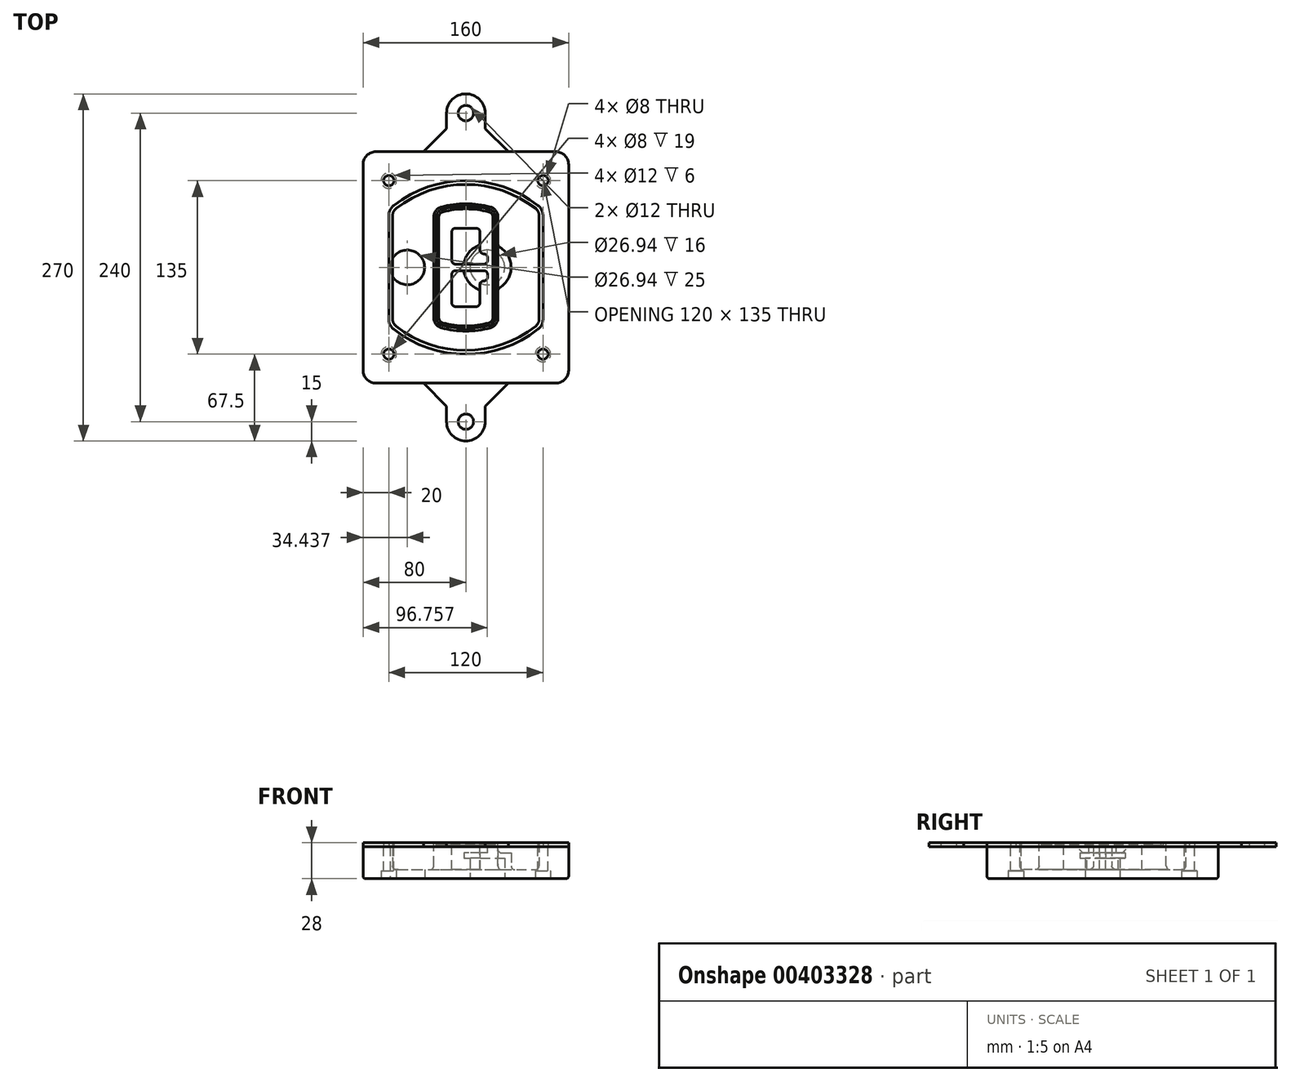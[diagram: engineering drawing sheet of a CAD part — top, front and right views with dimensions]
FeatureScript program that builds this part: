
annotation { "Feature Type Name" : "Feature", "Feature Type Description" : "" }
export const myFeature = defineFeature(function(context is Context, id is Id, definition is map)
    precondition{}
    {
        {
            var Q0;
            Q0=qCreatedBy(makeId("Top.planeOp"),FACE);
            var sketch = newSketch(context, id + "F0", { "sketchPlane" : qUnion([Q0])});
            skPoint(sketch, "E0.rect.middle", {"position": v(0, 0) * mm});
            skLineSegment(sketch, "E1.bottom", {"start": v(-70, -90) * mm, "end": v(70, -90) * mm});
            skLineSegment(sketch, "E1.top", {"start": v(-70, 90) * mm, "end": v(70, 90) * mm});
            skLineSegment(sketch, "E1.left", {"start": v(-80, -80) * mm, "end": v(-80, 80) * mm});
            skLineSegment(sketch, "E1.right", {"start": v(80, -80) * mm, "end": v(80, 80) * mm});
            skLineSegment(sketch, "E2", {"start": v(-80, 90) * mm, "end": v(80, -90) * mm, "construction": true});
            skLineSegment(sketch, "E3", {"start": v(80, 90) * mm, "end": v(-80, -90) * mm, "construction": true});
            skCircle(sketch, "E4", {"center": v(-60, 67.5) * mm, "radius": 4 * mm});
            skCircle(sketch, "E5", {"center": v(60, 67.5) * mm, "radius": 4 * mm});
            skCircle(sketch, "E6", {"center": v(60, -67.5) * mm, "radius": 4 * mm});
            skCircle(sketch, "E7", {"center": v(-60, -67.5) * mm, "radius": 4 * mm});
            skLineSegment(sketch, "E8", {"start": v(-60, 67.5) * mm, "end": v(60, 67.5) * mm, "construction": true});
            skLineSegment(sketch, "E9", {"start": v(60, 67.5) * mm, "end": v(60, -67.5) * mm, "construction": true});
            skLineSegment(sketch, "E10", {"start": v(60, -67.5) * mm, "end": v(-60, -67.5) * mm, "construction": true});
            skLineSegment(sketch, "E11", {"start": v(-60, -67.5) * mm, "end": v(-60, 67.5) * mm, "construction": true});
            skLineSegment(sketch, "E12", {"start": v(-60, 40.3) * mm, "end": v(-60, -40.3) * mm});
            skLineSegment(sketch, "E13", {"start": v(60, 40.3) * mm, "end": v(60, -40.3) * mm});
            skArc(sketch, "E14", {"start": v(56.15, 48.18) * mm, "mid": v(0, 67.5) * mm, "end": v(-56.15, 48.18) * mm});
            skArc(sketch, "E15", {"start": v(-56.15, -48.18) * mm, "mid": v(0, -67.5) * mm, "end": v(56.15, -48.18) * mm});
            skLineSegment(sketch, "E16", {"start": v(-60, 0) * mm, "end": v(60, 0) * mm, "construction": true});
            skPoint(sketch, "E17.visualSharp", {"position": v(-60, -45) * mm});
            skArc(sketch, "E17.filletArc", {"start": v(-60, -40.3) * mm, "mid": v(-58.99, -44.68) * mm, "end": v(-56.15, -48.18) * mm});
            skPoint(sketch, "E18.visualSharp", {"position": v(-60, 45) * mm});
            skArc(sketch, "E18.filletArc", {"start": v(-56.15, 48.18) * mm, "mid": v(-58.99, 44.68) * mm, "end": v(-60, 40.3) * mm});
            skPoint(sketch, "E19.visualSharp", {"position": v(60, 45) * mm});
            skArc(sketch, "E19.filletArc", {"start": v(60, 40.3) * mm, "mid": v(58.99, 44.68) * mm, "end": v(56.15, 48.18) * mm});
            skPoint(sketch, "E20.visualSharp", {"position": v(60, -45) * mm});
            skArc(sketch, "E20.filletArc", {"start": v(56.15, -48.18) * mm, "mid": v(58.99, -44.68) * mm, "end": v(60, -40.3) * mm});
            skPoint(sketch, "E21.visualSharp", {"position": v(-80, 90) * mm});
            skArc(sketch, "E21.filletArc", {"start": v(-70, 90) * mm, "mid": v(-77.07, 87.07) * mm, "end": v(-80, 80) * mm});
            skPoint(sketch, "E22.visualSharp", {"position": v(80, 90) * mm});
            skArc(sketch, "E22.filletArc", {"start": v(80, 80) * mm, "mid": v(77.07, 87.07) * mm, "end": v(70, 90) * mm});
            skPoint(sketch, "E23.visualSharp", {"position": v(80, -90) * mm});
            skArc(sketch, "E23.filletArc", {"start": v(70, -90) * mm, "mid": v(77.07, -87.07) * mm, "end": v(80, -80) * mm});
            skPoint(sketch, "E24.visualSharp", {"position": v(-80, -90) * mm});
            skArc(sketch, "E24.filletArc", {"start": v(-80, -80) * mm, "mid": v(-77.07, -87.07) * mm, "end": v(-70, -90) * mm});
            skArc(sketch, "E25.0", {"start": v(57, 40.3) * mm, "mid": v(56.3, 43.36) * mm, "end": v(54.3, 45.81) * mm});
            skLineSegment(sketch, "E25.1", {"start": v(57, 40.3) * mm, "end": v(57, -40.3) * mm});
            skArc(sketch, "E25.2", {"start": v(54.3, -45.81) * mm, "mid": v(56.3, -43.36) * mm, "end": v(57, -40.3) * mm});
            skArc(sketch, "E25.3", {"start": v(-54.3, -45.81) * mm, "mid": v(0, -64.5) * mm, "end": v(54.3, -45.81) * mm});
            skArc(sketch, "E25.4", {"start": v(-57, -40.3) * mm, "mid": v(-56.3, -43.36) * mm, "end": v(-54.3, -45.81) * mm});
            skArc(sketch, "E25.5", {"start": v(54.3, 45.81) * mm, "mid": v(0, 64.5) * mm, "end": v(-54.3, 45.81) * mm});
            skLineSegment(sketch, "E25.6", {"start": v(-57, 40.3) * mm, "end": v(-57, -40.3) * mm});
            skArc(sketch, "E25.7", {"start": v(-54.3, 45.81) * mm, "mid": v(-56.3, 43.36) * mm, "end": v(-57, 40.3) * mm});
            skArc(sketch, "E26.0", {"start": v(-58.62, 51.33) * mm, "mid": v(-62.58, 46.43) * mm, "end": v(-64, 40.3) * mm});
            skArc(sketch, "E26.1", {"start": v(58.62, 51.33) * mm, "mid": v(0, 71.5) * mm, "end": v(-58.62, 51.33) * mm});
            skArc(sketch, "E26.2", {"start": v(64, 40.3) * mm, "mid": v(62.58, 46.43) * mm, "end": v(58.62, 51.33) * mm});
            skLineSegment(sketch, "E26.3", {"start": v(64, 40.3) * mm, "end": v(64, -40.3) * mm});
            skArc(sketch, "E26.4", {"start": v(58.62, -51.33) * mm, "mid": v(62.58, -46.43) * mm, "end": v(64, -40.3) * mm});
            skLineSegment(sketch, "E26.5", {"start": v(-64, 40.3) * mm, "end": v(-64, -40.3) * mm});
            skArc(sketch, "E26.6", {"start": v(-58.62, -51.33) * mm, "mid": v(0, -71.5) * mm, "end": v(58.62, -51.33) * mm});
            skArc(sketch, "E26.7", {"start": v(-64, -40.3) * mm, "mid": v(-62.58, -46.43) * mm, "end": v(-58.62, -51.33) * mm});
            skSolve(sketch);
        }
        {
            var Q0;
            Q0=makeQuery(id+"F0.imprint","IMPRINT",FACE,{"disambiguationData":[TD([[makeQuery(id+"F0.imprint","IMPRINT",EDGE,{"derivedFrom":sQuery(id+"F0.wireOp",EDGE,"E1.bottom")}),1.0]])]});
            var Q1;
            Q1=makeQuery(id+"F0.imprint","IMPRINT",FACE,{"disambiguationData":[TD([[makeQuery(id+"F0.imprint","IMPRINT",EDGE,{"derivedFrom":sQuery(id+"F0.wireOp",EDGE,"E12")}),1.0]])]});
            var Q2;
            Q2=makeQuery(id+"F0.imprint","IMPRINT",FACE,{"disambiguationData":[TD([[makeQuery(id+"F0.imprint","IMPRINT",EDGE,{"derivedFrom":sQuery(id+"F0.wireOp",EDGE,"E25.0")}),1.0]])]});
            var Q3;
            Q3=makeQuery(id+"F0.imprint","IMPRINT",FACE,{"disambiguationData":[TD([[makeQuery(id+"F0.imprint","IMPRINT",EDGE,{"derivedFrom":sQuery(id+"F0.wireOp",EDGE,"E12")}),-1.0]])]});
            extrude(context, id + "F1", {"entities" : qUnion([Q0, Q1, Q2, Q3]), "oppositeDirection" : true, "depth" : 25 * mm});
        }
        {
            var Q0;
            Q0=makeQuery(id+"F0.imprint","IMPRINT",FACE,{"disambiguationData":[TD([[makeQuery(id+"F0.imprint","IMPRINT",EDGE,{"derivedFrom":sQuery(id+"F0.wireOp",EDGE,"E12")}),1.0]])]});
            extrude(context, id + "F2", {"entities" : qUnion([Q0]), "operationType" : NewBodyOperationType.ADD, "depth" : 3 * mm});
        }
        {
            var Q0;
            Q0=makeQuery(id+"F0.imprint","IMPRINT",FACE,{"disambiguationData":[TD([[makeQuery(id+"F0.imprint","IMPRINT",EDGE,{"derivedFrom":sQuery(id+"F0.wireOp",EDGE,"E25.0")}),1.0]])]});
            extrude(context, id + "F3", {"entities" : qUnion([Q0]), "operationType" : NewBodyOperationType.REMOVE, "oppositeDirection" : true, "depth" : 18 * mm});
        }
        {
            var Q0;
            Q0=makeQuery(id+"F2.opExtrude","CAP_FACE",FACE,{"disambiguationData":[OSD([sQuery(id+"F0.wireOp",EDGE,"E12"),sQuery(id+"F0.wireOp",EDGE,"E13"),sQuery(id+"F0.wireOp",EDGE,"E14"),sQuery(id+"F0.wireOp",EDGE,"E15"),sQuery(id+"F0.wireOp",EDGE,"E17.filletArc"),sQuery(id+"F0.wireOp",EDGE,"E18.filletArc"),sQuery(id+"F0.wireOp",EDGE,"E19.filletArc"),sQuery(id+"F0.wireOp",EDGE,"E20.filletArc"),sQuery(id+"F0.wireOp",EDGE,"E25.0"),sQuery(id+"F0.wireOp",EDGE,"E25.1"),sQuery(id+"F0.wireOp",EDGE,"E25.2"),sQuery(id+"F0.wireOp",EDGE,"E25.3"),sQuery(id+"F0.wireOp",EDGE,"E25.4"),sQuery(id+"F0.wireOp",EDGE,"E25.5"),sQuery(id+"F0.wireOp",EDGE,"E25.6"),sQuery(id+"F0.wireOp",EDGE,"E25.7")])],"isStart":false});
            var sketch = newSketch(context, id + "F4", { "sketchPlane" : qUnion([Q0])});
            skArc(sketch, "E27.0", {"start": v(-19.08, -46.97) * mm, "mid": v(0, -49.5) * mm, "end": v(19.08, -46.97) * mm});
            skArc(sketch, "E28.0", {"start": v(19.08, 46.97) * mm, "mid": v(0, 49.5) * mm, "end": v(-19.08, 46.97) * mm});
            skLineSegment(sketch, "E29", {"start": v(-25, 39.25) * mm, "end": v(-25, -39.25) * mm});
            skLineSegment(sketch, "E30", {"start": v(25, 39.25) * mm, "end": v(25, -39.25) * mm});
            skLineSegment(sketch, "E31", {"start": v(-25, 45.1) * mm, "end": v(25, 45.1) * mm, "construction": true});
            skLineSegment(sketch, "E32", {"start": v(-25, -45.1) * mm, "end": v(25, -45.1) * mm, "construction": true});
            skPoint(sketch, "E33.visualSharp", {"position": v(-25, 45.1) * mm});
            skArc(sketch, "E33.filletArc", {"start": v(-19.08, 46.97) * mm, "mid": v(-23.35, 44.11) * mm, "end": v(-25, 39.25) * mm});
            skPoint(sketch, "E34.visualSharp", {"position": v(25, 45.1) * mm});
            skArc(sketch, "E34.filletArc", {"start": v(25, 39.25) * mm, "mid": v(23.35, 44.11) * mm, "end": v(19.08, 46.97) * mm});
            skPoint(sketch, "E35.visualSharp", {"position": v(25, -45.1) * mm});
            skArc(sketch, "E35.filletArc", {"start": v(19.08, -46.97) * mm, "mid": v(23.35, -44.11) * mm, "end": v(25, -39.25) * mm});
            skPoint(sketch, "E36.visualSharp", {"position": v(-25, -45.1) * mm});
            skArc(sketch, "E36.filletArc", {"start": v(-25, -39.25) * mm, "mid": v(-23.35, -44.11) * mm, "end": v(-19.08, -46.97) * mm});
            skArc(sketch, "E37.0", {"start": v(54.3, 45.81) * mm, "mid": v(0, 64.5) * mm, "end": v(-54.3, 45.81) * mm});
            skArc(sketch, "E37.1", {"start": v(-54.3, 45.81) * mm, "mid": v(-56.3, 43.36) * mm, "end": v(-57, 40.3) * mm});
            skLineSegment(sketch, "E37.2", {"start": v(-57, 40.3) * mm, "end": v(-57, -40.3) * mm});
            skArc(sketch, "E37.3", {"start": v(-57, -40.3) * mm, "mid": v(-56.3, -43.36) * mm, "end": v(-54.3, -45.81) * mm});
            skArc(sketch, "E37.4", {"start": v(-54.3, -45.81) * mm, "mid": v(0, -64.5) * mm, "end": v(54.3, -45.81) * mm});
            skArc(sketch, "E37.5", {"start": v(54.3, -45.81) * mm, "mid": v(56.3, -43.36) * mm, "end": v(57, -40.3) * mm});
            skLineSegment(sketch, "E37.6", {"start": v(57, 40.3) * mm, "end": v(57, -40.3) * mm});
            skArc(sketch, "E37.7", {"start": v(57, 40.3) * mm, "mid": v(56.3, 43.36) * mm, "end": v(54.3, 45.81) * mm});
            skLineSegment(sketch, "E38.0", {"start": v(23, 39.25) * mm, "end": v(23, -39.25) * mm});
            skArc(sketch, "E38.1", {"start": v(18.56, -45.04) * mm, "mid": v(21.76, -42.9) * mm, "end": v(23, -39.25) * mm});
            skArc(sketch, "E38.2", {"start": v(-18.56, -45.04) * mm, "mid": v(0, -47.5) * mm, "end": v(18.56, -45.04) * mm});
            skArc(sketch, "E38.3", {"start": v(-23, -39.25) * mm, "mid": v(-21.76, -42.9) * mm, "end": v(-18.56, -45.04) * mm});
            skLineSegment(sketch, "E38.4", {"start": v(-23, 39.25) * mm, "end": v(-23, -39.25) * mm});
            skArc(sketch, "E38.5", {"start": v(23, 39.25) * mm, "mid": v(21.76, 42.9) * mm, "end": v(18.56, 45.04) * mm});
            skArc(sketch, "E38.6", {"start": v(-18.56, 45.04) * mm, "mid": v(-21.76, 42.9) * mm, "end": v(-23, 39.25) * mm});
            skArc(sketch, "E38.7", {"start": v(18.56, 45.04) * mm, "mid": v(0, 47.5) * mm, "end": v(-18.56, 45.04) * mm});
            skArc(sketch, "E39.0", {"start": v(21, 39.25) * mm, "mid": v(20.18, 41.68) * mm, "end": v(18.04, 43.1) * mm});
            skLineSegment(sketch, "E39.1", {"start": v(21, 39.25) * mm, "end": v(21, -39.25) * mm});
            skArc(sketch, "E39.2", {"start": v(18.04, -43.1) * mm, "mid": v(20.18, -41.68) * mm, "end": v(21, -39.25) * mm});
            skArc(sketch, "E39.3", {"start": v(-18.04, -43.1) * mm, "mid": v(0, -45.5) * mm, "end": v(18.04, -43.1) * mm});
            skArc(sketch, "E39.4", {"start": v(-21, -39.25) * mm, "mid": v(-20.18, -41.68) * mm, "end": v(-18.04, -43.1) * mm});
            skArc(sketch, "E39.5", {"start": v(18.04, 43.1) * mm, "mid": v(0, 45.5) * mm, "end": v(-18.04, 43.1) * mm});
            skLineSegment(sketch, "E39.6", {"start": v(-21, 39.25) * mm, "end": v(-21, -39.25) * mm});
            skArc(sketch, "E39.7", {"start": v(-18.04, 43.1) * mm, "mid": v(-20.18, 41.68) * mm, "end": v(-21, 39.25) * mm});
            skLineSegment(sketch, "E40", {"start": v(-25, 0) * mm, "end": v(25, 0) * mm, "construction": true});
            skLineSegment(sketch, "E41", {"start": v(-11, 5.5) * mm, "end": v(-11, 27.5) * mm});
            skLineSegment(sketch, "E42", {"start": v(-8, 30.5) * mm, "end": v(8, 30.5) * mm});
            skLineSegment(sketch, "E43", {"start": v(11, 27.5) * mm, "end": v(11, 13.5) * mm});
            skLineSegment(sketch, "E44", {"start": v(14, 10.5) * mm, "end": v(14, 10.5) * mm});
            skLineSegment(sketch, "E45", {"start": v(17, 7.5) * mm, "end": v(17, 5.5) * mm});
            skLineSegment(sketch, "E46", {"start": v(14, 2.5) * mm, "end": v(-8, 2.5) * mm});
            skPoint(sketch, "E47.visualSharp", {"position": v(-11, 30.5) * mm});
            skArc(sketch, "E47.filletArc", {"start": v(-8, 30.5) * mm, "mid": v(-10.12, 29.62) * mm, "end": v(-11, 27.5) * mm});
            skPoint(sketch, "E48.visualSharp", {"position": v(11, 30.5) * mm});
            skArc(sketch, "E48.filletArc", {"start": v(11, 27.5) * mm, "mid": v(10.12, 29.62) * mm, "end": v(8, 30.5) * mm});
            skPoint(sketch, "E49.visualSharp", {"position": v(11, 10.5) * mm});
            skArc(sketch, "E49.filletArc", {"start": v(11, 13.5) * mm, "mid": v(11.88, 11.38) * mm, "end": v(14, 10.5) * mm});
            skPoint(sketch, "E50.visualSharp", {"position": v(17, 10.5) * mm});
            skArc(sketch, "E50.filletArc", {"start": v(17, 7.5) * mm, "mid": v(16.12, 9.62) * mm, "end": v(14, 10.5) * mm});
            skPoint(sketch, "E51.visualSharp", {"position": v(17, 2.5) * mm});
            skArc(sketch, "E51.filletArc", {"start": v(14, 2.5) * mm, "mid": v(16.12, 3.38) * mm, "end": v(17, 5.5) * mm});
            skPoint(sketch, "E52.visualSharp", {"position": v(-11, 2.5) * mm});
            skArc(sketch, "E52.filletArc", {"start": v(-11, 5.5) * mm, "mid": v(-10.12, 3.38) * mm, "end": v(-8, 2.5) * mm});
            skLineSegment(sketch, "E53.0.MirrorCS", {"start": v(14, -2.5) * mm, "end": v(-8, -2.5) * mm});
            skArc(sketch, "E54.0.MirrorCS", {"start": v(-11, -5.5) * mm, "mid": v(-10.12, -3.38) * mm, "end": v(-8, -2.5) * mm});
            skLineSegment(sketch, "E55.0.MirrorCS", {"start": v(-11, -5.5) * mm, "end": v(-11, -27.5) * mm});
            skArc(sketch, "E56.0.MirrorCS", {"start": v(-8, -30.5) * mm, "mid": v(-10.12, -29.62) * mm, "end": v(-11, -27.5) * mm});
            skLineSegment(sketch, "E57.0.MirrorCS", {"start": v(-8, -30.5) * mm, "end": v(8, -30.5) * mm});
            skArc(sketch, "E58.0.MirrorCS", {"start": v(11, -27.5) * mm, "mid": v(10.12, -29.62) * mm, "end": v(8, -30.5) * mm});
            skLineSegment(sketch, "E59.0.MirrorCS", {"start": v(11, -27.5) * mm, "end": v(11, -13.5) * mm});
            skArc(sketch, "E60.0.MirrorCS", {"start": v(11, -13.5) * mm, "mid": v(11.88, -11.38) * mm, "end": v(14, -10.5) * mm});
            skArc(sketch, "E61.0.MirrorCS", {"start": v(17, -7.5) * mm, "mid": v(16.12, -9.62) * mm, "end": v(14, -10.5) * mm});
            skLineSegment(sketch, "E62.0.MirrorCS", {"start": v(17, -7.5) * mm, "end": v(17, -5.5) * mm});
            skArc(sketch, "E63.0.MirrorCS", {"start": v(14, -2.5) * mm, "mid": v(16.12, -3.38) * mm, "end": v(17, -5.5) * mm});
            skSolve(sketch);
        }
        {
            var Q0;
            Q0=makeQuery(id+"F4.imprint","IMPRINT",FACE,{"disambiguationData":[TD([[makeQuery(id+"F4.imprint","IMPRINT",EDGE,{"derivedFrom":sQuery(id+"F4.wireOp",EDGE,"E27.0")}),1.0]])]});
            var Q1;
            Q1=makeQuery(id+"F4.imprint","IMPRINT",FACE,{"disambiguationData":[TD([[makeQuery(id+"F4.imprint","IMPRINT",EDGE,{"derivedFrom":sQuery(id+"F4.wireOp",EDGE,"E38.0")}),-1.0]])]});
            var Q2;
            Q2=makeQuery(id+"F4.imprint","IMPRINT",FACE,{"disambiguationData":[TD([[makeQuery(id+"F4.imprint","IMPRINT",EDGE,{"derivedFrom":sQuery(id+"F4.wireOp",EDGE,"E39.0")}),1.0]])]});
            extrude(context, id + "F5", {"entities" : qUnion([Q0, Q1, Q2]), "operationType" : NewBodyOperationType.ADD, "endBound" : BoundingType.UP_TO_NEXT, "oppositeDirection" : true, "depth" : 25 * mm});
        }
        {
            var Q0;
            Q0=makeQuery(id+"F4.imprint","IMPRINT",FACE,{"disambiguationData":[TD([[makeQuery(id+"F4.imprint","IMPRINT",EDGE,{"derivedFrom":sQuery(id+"F4.wireOp",EDGE,"E38.0")}),-1.0]])]});
            extrude(context, id + "F6", {"entities" : qUnion([Q0]), "operationType" : NewBodyOperationType.REMOVE, "oppositeDirection" : true, "depth" : 2 * mm});
        }
        {
            var Q0;
            Q0=makeQuery(id+"F1.opExtrude","CAP_FACE",FACE,{"disambiguationData":[OSD([sQuery(id+"F0.wireOp",EDGE,"E1.bottom"),sQuery(id+"F0.wireOp",EDGE,"E1.top"),sQuery(id+"F0.wireOp",EDGE,"E1.left"),sQuery(id+"F0.wireOp",EDGE,"E1.right"),sQuery(id+"F0.wireOp",EDGE,"E4"),sQuery(id+"F0.wireOp",EDGE,"E5"),sQuery(id+"F0.wireOp",EDGE,"E6"),sQuery(id+"F0.wireOp",EDGE,"E7"),sQuery(id+"F0.wireOp",EDGE,"E21.filletArc"),sQuery(id+"F0.wireOp",EDGE,"E22.filletArc"),sQuery(id+"F0.wireOp",EDGE,"E23.filletArc"),sQuery(id+"F0.wireOp",EDGE,"E24.filletArc")])],"isStart":false});
            var sketch = newSketch(context, id + "F7", { "sketchPlane" : qUnion([Q0])});
            skCircle(sketch, "E64", {"center": v(16.76, 0) * mm, "radius": 13.47 * mm});
            skCircle(sketch, "E65", {"center": v(-45.56, 0) * mm, "radius": 13.47 * mm});
            skLineSegment(sketch, "E66", {"start": v(80, 0) * mm, "end": v(-80, 0) * mm});
            skCircle(sketch, "E67", {"center": v(16.76, 0) * mm, "radius": 18.47 * mm});
            skCircle(sketch, "E68", {"center": v(60, -67.5) * mm, "radius": 6 * mm});
            skCircle(sketch, "E69", {"center": v(-60, -67.5) * mm, "radius": 6 * mm});
            skCircle(sketch, "E70", {"center": v(-60, 67.5) * mm, "radius": 6 * mm});
            skCircle(sketch, "E71", {"center": v(60, 67.5) * mm, "radius": 6 * mm});
            skSolve(sketch);
        }
        {
            var Q0;
            {var subQ1=sQuery(id+"F7.wireOp",EDGE,"E66");var subQ4=sQuery(id+"F7.wireOp",EDGE,"E64");var subQ6=makeQuery(id+"F7.imprint","INTERSECT",VERTEX,{"disambiguationData":[OD(0.0)],"derivedFrom":[subQ4,subQ1]});Q0=makeQuery(id+"F7.imprint","IMPRINT",FACE,{"disambiguationData":[TD([[makeQuery(id+"F7.imprint","IMPRINT",EDGE,{"disambiguationData":[TD([[subQ6,-1.0]])],"derivedFrom":subQ4}),-1.0]])]});}
            var Q1;
            {var subQ0=sQuery(id+"F7.wireOp",EDGE,"E66");var subQ1=sQuery(id+"F7.wireOp",EDGE,"E64");var subQ3=makeQuery(id+"F7.imprint","INTERSECT",VERTEX,{"disambiguationData":[OD(0.0)],"derivedFrom":[subQ1,subQ0]});Q1=makeQuery(id+"F7.imprint","IMPRINT",FACE,{"disambiguationData":[TD([[makeQuery(id+"F7.imprint","IMPRINT",EDGE,{"disambiguationData":[TD([[subQ3,-1.0]])],"derivedFrom":subQ1}),1.0]])]});}
            var Q2;
            {var subQ0=sQuery(id+"F7.wireOp",EDGE,"E66");var subQ1=sQuery(id+"F7.wireOp",EDGE,"E64");var subQ3=makeQuery(id+"F7.imprint","INTERSECT",VERTEX,{"disambiguationData":[OD(0.0)],"derivedFrom":[subQ1,subQ0]});Q2=makeQuery(id+"F7.imprint","IMPRINT",FACE,{"disambiguationData":[TD([[makeQuery(id+"F7.imprint","IMPRINT",EDGE,{"disambiguationData":[TD([[subQ3,1.0]])],"derivedFrom":subQ1}),1.0]])]});}
            var Q3;
            {var subQ1=sQuery(id+"F7.wireOp",EDGE,"E66");var subQ4=sQuery(id+"F7.wireOp",EDGE,"E64");var subQ6=makeQuery(id+"F7.imprint","INTERSECT",VERTEX,{"disambiguationData":[OD(0.0)],"derivedFrom":[subQ4,subQ1]});Q3=makeQuery(id+"F7.imprint","IMPRINT",FACE,{"disambiguationData":[TD([[makeQuery(id+"F7.imprint","IMPRINT",EDGE,{"disambiguationData":[TD([[subQ6,1.0]])],"derivedFrom":subQ4}),-1.0]])]});}
            extrude(context, id + "F8", {"entities" : qUnion([Q0, Q1, Q2, Q3]), "operationType" : NewBodyOperationType.ADD, "oppositeDirection" : true, "depth" : 20 * mm});
        }
        {
            var Q0;
            {var subQ0=sQuery(id+"F7.wireOp",EDGE,"E66");var subQ1=sQuery(id+"F7.wireOp",EDGE,"E64");var subQ3=makeQuery(id+"F7.imprint","INTERSECT",VERTEX,{"disambiguationData":[OD(0.0)],"derivedFrom":[subQ1,subQ0]});Q0=makeQuery(id+"F7.imprint","IMPRINT",FACE,{"disambiguationData":[TD([[makeQuery(id+"F7.imprint","IMPRINT",EDGE,{"disambiguationData":[TD([[subQ3,-1.0]])],"derivedFrom":subQ1}),1.0]])]});}
            var Q1;
            {var subQ0=sQuery(id+"F7.wireOp",EDGE,"E66");var subQ1=sQuery(id+"F7.wireOp",EDGE,"E64");var subQ3=makeQuery(id+"F7.imprint","INTERSECT",VERTEX,{"disambiguationData":[OD(0.0)],"derivedFrom":[subQ1,subQ0]});Q1=makeQuery(id+"F7.imprint","IMPRINT",FACE,{"disambiguationData":[TD([[makeQuery(id+"F7.imprint","IMPRINT",EDGE,{"disambiguationData":[TD([[subQ3,1.0]])],"derivedFrom":subQ1}),1.0]])]});}
            extrude(context, id + "F9", {"entities" : qUnion([Q0, Q1]), "operationType" : NewBodyOperationType.REMOVE, "oppositeDirection" : true, "depth" : 16 * mm});
        }
        {
            var Q0;
            {var subQ0=sQuery(id+"F7.wireOp",EDGE,"E66");var subQ1=sQuery(id+"F7.wireOp",EDGE,"E65");var subQ3=makeQuery(id+"F7.imprint","INTERSECT",VERTEX,{"disambiguationData":[OD(0.0)],"derivedFrom":[subQ1,subQ0]});Q0=makeQuery(id+"F7.imprint","IMPRINT",FACE,{"disambiguationData":[TD([[makeQuery(id+"F7.imprint","IMPRINT",EDGE,{"disambiguationData":[TD([[subQ3,-1.0]])],"derivedFrom":subQ1}),1.0]])]});}
            var Q1;
            {var subQ0=sQuery(id+"F7.wireOp",EDGE,"E66");var subQ1=sQuery(id+"F7.wireOp",EDGE,"E65");var subQ3=makeQuery(id+"F7.imprint","INTERSECT",VERTEX,{"disambiguationData":[OD(0.0)],"derivedFrom":[subQ1,subQ0]});Q1=makeQuery(id+"F7.imprint","IMPRINT",FACE,{"disambiguationData":[TD([[makeQuery(id+"F7.imprint","IMPRINT",EDGE,{"disambiguationData":[TD([[subQ3,1.0]])],"derivedFrom":subQ1}),1.0]])]});}
            extrude(context, id + "F10", {"entities" : qUnion([Q0, Q1]), "operationType" : NewBodyOperationType.REMOVE, "oppositeDirection" : true, "depth" : 25 * mm});
        }
        {
            var Q0;
            Q0=makeQuery(id+"F7.imprint","IMPRINT",FACE,{"disambiguationData":[TD([[makeQuery(id+"F7.imprint","IMPRINT",EDGE,{"derivedFrom":sQuery(id+"F7.wireOp",EDGE,"E68")}),1.0]])]});
            var Q1;
            Q1=makeQuery(id+"F7.imprint","IMPRINT",FACE,{"disambiguationData":[TD([[makeQuery(id+"F7.imprint","IMPRINT",EDGE,{"derivedFrom":makeQuery(id+"F1.opExtrude","CAP_EDGE",EDGE,{"disambiguationData":[OSD([sQuery(id+"F0.wireOp",EDGE,"E5")])],"isStart":false})}),-1.0]])]});
            var Q2;
            Q2=makeQuery(id+"F7.imprint","IMPRINT",FACE,{"disambiguationData":[TD([[makeQuery(id+"F7.imprint","IMPRINT",EDGE,{"derivedFrom":sQuery(id+"F7.wireOp",EDGE,"E69")}),1.0]])]});
            var Q3;
            Q3=makeQuery(id+"F7.imprint","IMPRINT",FACE,{"disambiguationData":[TD([[makeQuery(id+"F7.imprint","IMPRINT",EDGE,{"derivedFrom":makeQuery(id+"F1.opExtrude","CAP_EDGE",EDGE,{"disambiguationData":[OSD([sQuery(id+"F0.wireOp",EDGE,"E4")])],"isStart":false})}),-1.0]])]});
            var Q4;
            Q4=makeQuery(id+"F7.imprint","IMPRINT",FACE,{"disambiguationData":[TD([[makeQuery(id+"F7.imprint","IMPRINT",EDGE,{"derivedFrom":sQuery(id+"F7.wireOp",EDGE,"E70")}),1.0]])]});
            var Q5;
            Q5=makeQuery(id+"F7.imprint","IMPRINT",FACE,{"disambiguationData":[TD([[makeQuery(id+"F7.imprint","IMPRINT",EDGE,{"derivedFrom":makeQuery(id+"F1.opExtrude","CAP_EDGE",EDGE,{"disambiguationData":[OSD([sQuery(id+"F0.wireOp",EDGE,"E7")])],"isStart":false})}),-1.0]])]});
            var Q6;
            Q6=makeQuery(id+"F7.imprint","IMPRINT",FACE,{"disambiguationData":[TD([[makeQuery(id+"F7.imprint","IMPRINT",EDGE,{"derivedFrom":sQuery(id+"F7.wireOp",EDGE,"E71")}),1.0]])]});
            var Q7;
            Q7=makeQuery(id+"F7.imprint","IMPRINT",FACE,{"disambiguationData":[TD([[makeQuery(id+"F7.imprint","IMPRINT",EDGE,{"derivedFrom":makeQuery(id+"F1.opExtrude","CAP_EDGE",EDGE,{"disambiguationData":[OSD([sQuery(id+"F0.wireOp",EDGE,"E6")])],"isStart":false})}),-1.0]])]});
            extrude(context, id + "F11", {"entities" : qUnion([Q0, Q1, Q2, Q3, Q4, Q5, Q6, Q7]), "operationType" : NewBodyOperationType.REMOVE, "oppositeDirection" : true, "depth" : 6 * mm});
        }
        {
            var Q0;
            Q0=makeQuery(id+"F9.boolean.opBoolean","COPY",FACE,{"derivedFrom":makeQuery(id+"F9.opExtrude","CAP_FACE",FACE,{"disambiguationData":[OSD([sQuery(id+"F7.wireOp",EDGE,"E64")])],"isStart":false})});
            var sketch = newSketch(context, id + "F12", { "sketchPlane" : qUnion([Q0])});
            skArc(sketch, "E72.0", {"start": v(11, 17.55) * mm, "mid": v(2.57, 11.82) * mm, "end": v(-1.54, 2.5) * mm});
            skArc(sketch, "E72.1", {"start": v(-1.54, -2.5) * mm, "mid": v(2.57, -11.82) * mm, "end": v(11, -17.55) * mm});
            skLineSegment(sketch, "E73", {"start": v(-1.54, -2.5) * mm, "end": v(14, -2.5) * mm});
            skLineSegment(sketch, "E74.0", {"start": v(14, 2.5) * mm, "end": v(-1.54, 2.5) * mm});
            skArc(sketch, "E74.1", {"start": v(14, 2.5) * mm, "mid": v(16.12, 3.38) * mm, "end": v(17, 5.5) * mm});
            skLineSegment(sketch, "E74.2", {"start": v(17, 7.5) * mm, "end": v(17, 5.5) * mm});
            skArc(sketch, "E74.3", {"start": v(17, 7.5) * mm, "mid": v(16.12, 9.62) * mm, "end": v(14, 10.5) * mm});
            skArc(sketch, "E74.4", {"start": v(11, 13.5) * mm, "mid": v(11.88, 11.38) * mm, "end": v(14, 10.5) * mm});
            skLineSegment(sketch, "E74.5", {"start": v(11, 17.55) * mm, "end": v(11, 13.5) * mm});
            skLineSegment(sketch, "E74.7", {"start": v(14, -2.5) * mm, "end": v(-1.54, -2.5) * mm});
            skArc(sketch, "E74.8", {"start": v(14, -2.5) * mm, "mid": v(16.12, -3.38) * mm, "end": v(17, -5.5) * mm});
            skLineSegment(sketch, "E74.9", {"start": v(17, -7.5) * mm, "end": v(17, -5.5) * mm});
            skArc(sketch, "E74.10", {"start": v(17, -7.5) * mm, "mid": v(16.12, -9.62) * mm, "end": v(14, -10.5) * mm});
            skArc(sketch, "E74.11", {"start": v(11, -13.5) * mm, "mid": v(11.88, -11.38) * mm, "end": v(14, -10.5) * mm});
            skLineSegment(sketch, "E74.12", {"start": v(11, -17.55) * mm, "end": v(11, -13.5) * mm});
            skPoint(sketch, "E75.orphan", {"position": v(11, -27.5) * mm});
            skPoint(sketch, "E76.orphan", {"position": v(-8, -2.5) * mm});
            skPoint(sketch, "E77.orphan", {"position": v(-8, 2.5) * mm});
            skPoint(sketch, "E78.orphan", {"position": v(11, 27.5) * mm});
            skSolve(sketch);
        }
        {
            var Q0;
            {var subQ7=sQuery(id+"F12.wireOp",EDGE,"E72.0");var subQ14=sQuery(id+"F12.wireOp",EDGE,"E72.1");var subQ16=sQuery(id+"F12.wireOp",EDGE,"E74.1");var subQ18=sQuery(id+"F12.wireOp",EDGE,"E74.8");Q0=qUnion([makeQuery(id+"F12.imprint","IMPRINT",FACE,{"disambiguationData":[TD([[makeQuery(id+"F12.imprint","IMPRINT",EDGE,{"derivedFrom":subQ7}),1.0]])]}),makeQuery(id+"F12.imprint","IMPRINT",FACE,{"disambiguationData":[TD([[makeQuery(id+"F12.imprint","IMPRINT",EDGE,{"derivedFrom":subQ14}),1.0]])]}),makeQuery(id+"F12.imprint","IMPRINT",FACE,{"disambiguationData":[TD([[makeQuery(id+"F12.imprint","IMPRINT",EDGE,{"derivedFrom":subQ16}),1.0]])]}),makeQuery(id+"F12.imprint","IMPRINT",FACE,{"disambiguationData":[TD([[makeQuery(id+"F12.imprint","IMPRINT",EDGE,{"derivedFrom":subQ18}),-1.0]])]})]);}
            var Q1;
            Q1=makeQuery(id+"F5.boolean.opBoolean","SPLIT",FACE,{"disambiguationData":[TD([makeQuery(id+"F5.opExtrude","SWEPT_FACE",FACE,{"disambiguationData":[OSD([sQuery(id+"F4.wireOp",EDGE,"E41")])]})])],"derivedFrom":makeQuery(id+"F3.boolean.opBoolean","COPY",FACE,{"derivedFrom":makeQuery(id+"F3.opExtrude","CAP_FACE",FACE,{"disambiguationData":[OSD([sQuery(id+"F0.wireOp",EDGE,"E25.0"),sQuery(id+"F0.wireOp",EDGE,"E25.1"),sQuery(id+"F0.wireOp",EDGE,"E25.2"),sQuery(id+"F0.wireOp",EDGE,"E25.3"),sQuery(id+"F0.wireOp",EDGE,"E25.4"),sQuery(id+"F0.wireOp",EDGE,"E25.5"),sQuery(id+"F0.wireOp",EDGE,"E25.6"),sQuery(id+"F0.wireOp",EDGE,"E25.7")])],"isStart":false})})});
            extrude(context, id + "F13", {"entities" : qUnion([Q0]), "operationType" : NewBodyOperationType.REMOVE, "endBound" : BoundingType.UP_TO_SURFACE, "endBoundEntityFace" : qUnion([Q1]), "depth" : 25 * mm});
        }
        {
            var Q0;
            Q0=makeQuery(id+"F3.boolean.opBoolean","COPY",EDGE,{"derivedFrom":makeQuery(id+"F3.opExtrude","CAP_EDGE",EDGE,{"disambiguationData":[OSD([sQuery(id+"F0.wireOp",EDGE,"E25.6")])],"isStart":false})});
            var Q1;
            Q1=makeQuery(id+"F8.boolean.opBoolean","INTERSECT",EDGE,{"derivedFrom":[makeQuery(id+"F5.opExtrude","SWEPT_FACE",FACE,{"disambiguationData":[OSD([sQuery(id+"F4.wireOp",EDGE,"E30")])]}),makeQuery(id+"F8.opExtrude","CAP_FACE",FACE,{"disambiguationData":[OSD([sQuery(id+"F7.wireOp",EDGE,"E67")])],"isStart":false})]});
            var Q2;
            Q2=makeQuery(id+"F8.boolean.opBoolean","INTERSECT",EDGE,{"disambiguationData":[OD(1.0)],"derivedFrom":[makeQuery(id+"F5.opExtrude","SWEPT_FACE",FACE,{"disambiguationData":[OSD([sQuery(id+"F4.wireOp",EDGE,"E30")])]}),makeQuery(id+"F8.opExtrude","SWEPT_FACE",FACE,{"disambiguationData":[OSD([sQuery(id+"F7.wireOp",EDGE,"E67")])]})]});
            var Q3;
            {var subQ0=sQuery(id+"F4.wireOp",EDGE,"E30");Q3=makeQuery(id+"F8.boolean.opBoolean","SPLIT",EDGE,{"disambiguationData":[TD([makeQuery(id+"F5.opExtrude","SWEPT_FACE",FACE,{"disambiguationData":[OSD([sQuery(id+"F4.wireOp",EDGE,"E35.filletArc")])]})])],"derivedFrom":makeQuery(id+"F5.opExtrude","CAP_EDGE",EDGE,{"disambiguationData":[OSD([subQ0])],"isStart":false})});}
            var Q4;
            {var subQ0=sQuery(id+"F0.wireOp",EDGE,"E25.7");var subQ1=sQuery(id+"F0.wireOp",EDGE,"E25.1");var subQ2=sQuery(id+"F0.wireOp",EDGE,"E25.6");var subQ3=sQuery(id+"F0.wireOp",EDGE,"E25.5");var subQ4=sQuery(id+"F0.wireOp",EDGE,"E25.4");var subQ5=sQuery(id+"F0.wireOp",EDGE,"E25.0");var subQ6=sQuery(id+"F0.wireOp",EDGE,"E25.2");var subQ7=sQuery(id+"F0.wireOp",EDGE,"E25.3");Q4=makeQuery(id+"F8.boolean.opBoolean","INTERSECT",EDGE,{"derivedFrom":[makeQuery(id+"F5.boolean.opBoolean","SPLIT",FACE,{"disambiguationData":[TD([makeQuery(id+"F2.opExtrude","SWEPT_FACE",FACE,{"disambiguationData":[OSD([subQ5])]})])],"derivedFrom":makeQuery(id+"F3.boolean.opBoolean","COPY",FACE,{"derivedFrom":makeQuery(id+"F3.opExtrude","CAP_FACE",FACE,{"disambiguationData":[OSD([subQ5,subQ1,subQ6,subQ7,subQ4,subQ3,subQ2,subQ0])],"isStart":false})})}),makeQuery(id+"F8.opExtrude","SWEPT_FACE",FACE,{"disambiguationData":[OSD([sQuery(id+"F7.wireOp",EDGE,"E67")])]})]});}
            var Q5;
            Q5=makeQuery(id+"F8.boolean.opBoolean","INTERSECT",EDGE,{"disambiguationData":[OD(0.0)],"derivedFrom":[makeQuery(id+"F5.opExtrude","SWEPT_FACE",FACE,{"disambiguationData":[OSD([sQuery(id+"F4.wireOp",EDGE,"E30")])]}),makeQuery(id+"F8.opExtrude","SWEPT_FACE",FACE,{"disambiguationData":[OSD([sQuery(id+"F7.wireOp",EDGE,"E67")])]})]});
            fillet(context, id + "F14", {"entities" : qUnion([Q0, Q1, Q2, Q3, Q4, Q5]), "radius" : 3 * mm, "tangentPropagation" : true, "allowEdgeOverflow" : false});
        }
        {
            var Q0;
            Q0=makeQuery(id+"F1.opExtrude","CAP_EDGE",EDGE,{"disambiguationData":[OSD([sQuery(id+"F0.wireOp",EDGE,"E1.bottom")])],"isStart":false});
            fillet(context, id + "F15", {"entities" : qUnion([Q0]), "radius" : 2 * mm, "tangentPropagation" : true, "allowEdgeOverflow" : false});
        }
        {
            var Q0;
            {var subQ0=sQuery(id+"F0.wireOp",EDGE,"E21.filletArc");var subQ1=sQuery(id+"F0.wireOp",EDGE,"E7");var subQ2=sQuery(id+"F0.wireOp",EDGE,"E6");var subQ3=sQuery(id+"F0.wireOp",EDGE,"E5");var subQ4=sQuery(id+"F0.wireOp",EDGE,"E4");var subQ5=sQuery(id+"F0.wireOp",EDGE,"E22.filletArc");var subQ6=sQuery(id+"F0.wireOp",EDGE,"E1.bottom");var subQ7=sQuery(id+"F0.wireOp",EDGE,"E1.right");var subQ8=sQuery(id+"F0.wireOp",EDGE,"E1.top");var subQ9=sQuery(id+"F0.wireOp",EDGE,"E1.left");var subQ10=sQuery(id+"F0.wireOp",EDGE,"E23.filletArc");var subQ11=sQuery(id+"F0.wireOp",EDGE,"E24.filletArc");Q0=makeQuery(id+"F2.boolean.opBoolean","SPLIT",FACE,{"disambiguationData":[TD([makeQuery(id+"F1.opExtrude","SWEPT_FACE",FACE,{"disambiguationData":[OSD([subQ6])]})])],"derivedFrom":makeQuery(id+"F1.opExtrude","CAP_FACE",FACE,{"disambiguationData":[OSD([subQ6,subQ8,subQ9,subQ7,subQ4,subQ3,subQ2,subQ1,subQ0,subQ5,subQ10,subQ11])],"isStart":true})});}
            var sketch = newSketch(context, id + "F16", { "sketchPlane" : qUnion([Q0])});
            skSolve(sketch);
        }
        {
            var Q0;
            Q0=makeQuery(id+"F16.imprint","IMPRINT",FACE,{"disambiguationData":[TD([[makeQuery(id+"F16.imprint","IMPRINT",EDGE,{"derivedFrom":makeQuery(id+"F1.opExtrude","CAP_EDGE",EDGE,{"disambiguationData":[OSD([sQuery(id+"F0.wireOp",EDGE,"E1.bottom")])],"isStart":true})}),1.0]])]});
            var sketch = newSketch(context, id + "F17", { "sketchPlane" : qUnion([Q0])});
            skLineSegment(sketch, "E79.0.0", {"start": v(70, 90) * mm, "end": v(-70, 90) * mm});
            skArc(sketch, "E79.0.1", {"start": v(-70, 90) * mm, "mid": v(-77.07, 87.07) * mm, "end": v(-80, 80) * mm});
            skLineSegment(sketch, "E79.0.2", {"start": v(-80, 80) * mm, "end": v(-80, -80) * mm});
            skArc(sketch, "E79.0.3", {"start": v(-80, -80) * mm, "mid": v(-77.07, -87.07) * mm, "end": v(-70, -90) * mm});
            skLineSegment(sketch, "E79.0.4", {"start": v(-70, -90) * mm, "end": v(70, -90) * mm});
            skArc(sketch, "E79.0.5", {"start": v(70, -90) * mm, "mid": v(77.07, -87.07) * mm, "end": v(80, -80) * mm});
            skLineSegment(sketch, "E79.0.6", {"start": v(80, -80) * mm, "end": v(80, 80) * mm});
            skArc(sketch, "E79.0.7", {"start": v(80, 80) * mm, "mid": v(77.07, 87.07) * mm, "end": v(70, 90) * mm});
            skLineSegment(sketch, "E80", {"start": v(0, 90) * mm, "end": v(0, 120) * mm, "construction": true});
            skLineSegment(sketch, "E81", {"start": v(-33, 90) * mm, "end": v(-15, 108) * mm});
            skLineSegment(sketch, "E82", {"start": v(-15, 108) * mm, "end": v(-15, 120) * mm});
            skLineSegment(sketch, "E83", {"start": v(33, 90) * mm, "end": v(15, 108) * mm});
            skLineSegment(sketch, "E84", {"start": v(15, 108) * mm, "end": v(15, 120) * mm});
            skCircle(sketch, "E85", {"center": v(0, 120) * mm, "radius": 6 * mm});
            skArc(sketch, "E86", {"start": v(15, 120) * mm, "mid": v(0, 135) * mm, "end": v(-15, 120) * mm});
            skLineSegment(sketch, "E87", {"start": v(-80, 0) * mm, "end": v(80, 0) * mm, "construction": true});
            skArc(sketch, "E88.MirrorCS", {"start": v(-15, 120) * mm, "mid": v(0, 135) * mm, "end": v(15, 120) * mm});
            skLineSegment(sketch, "E89.MirrorCS", {"start": v(80, 0) * mm, "end": v(-80, 0) * mm});
            skLineSegment(sketch, "E90.MirrorCS", {"start": v(-33, -90) * mm, "end": v(-15, -108) * mm});
            skLineSegment(sketch, "E91.MirrorCS", {"start": v(-15, -108) * mm, "end": v(-15, -120) * mm});
            skArc(sketch, "E92.MirrorCS", {"start": v(-15, -120) * mm, "mid": v(0, -135) * mm, "end": v(15, -120) * mm});
            skCircle(sketch, "E93.MirrorC", {"center": v(0, -120) * mm, "radius": 6 * mm});
            skLineSegment(sketch, "E94.MirrorCS", {"start": v(0, -90) * mm, "end": v(0, -120) * mm, "construction": true});
            skLineSegment(sketch, "E95.MirrorCS", {"start": v(15, -108) * mm, "end": v(15, -120) * mm});
            skLineSegment(sketch, "E96.MirrorCS", {"start": v(33, -90) * mm, "end": v(15, -108) * mm});
            skSolve(sketch);
        }
        {
            var Q0;
            Q0=makeQuery(id+"F17.imprint","IMPRINT",FACE,{"disambiguationData":[TD([[makeQuery(id+"F17.imprint","IMPRINT",EDGE,{"derivedFrom":sQuery(id+"F17.wireOp",EDGE,"E85")}),-1.0]])]});
            var Q1;
            Q1=makeQuery(id+"F16.imprint","IMPRINT",FACE,{"disambiguationData":[TD([[makeQuery(id+"F16.imprint","IMPRINT",EDGE,{"derivedFrom":makeQuery(id+"F1.opExtrude","CAP_EDGE",EDGE,{"disambiguationData":[OSD([sQuery(id+"F0.wireOp",EDGE,"E1.bottom")])],"isStart":true})}),1.0]])]});
            var Q2;
            {var subQ0=sQuery(id+"F17.wireOp",EDGE,"E90.MirrorCS");Q2=makeQuery(id+"F17.imprint","IMPRINT",FACE,{"disambiguationData":[TD([[makeQuery(id+"F17.imprint","IMPRINT",EDGE,{"derivedFrom":subQ0}),1.0]])]});}
            var Q3;
            Q3=makeQuery(id+"F2.opExtrude","CAP_FACE",FACE,{"disambiguationData":[OSD([sQuery(id+"F0.wireOp",EDGE,"E12"),sQuery(id+"F0.wireOp",EDGE,"E13"),sQuery(id+"F0.wireOp",EDGE,"E14"),sQuery(id+"F0.wireOp",EDGE,"E15"),sQuery(id+"F0.wireOp",EDGE,"E17.filletArc"),sQuery(id+"F0.wireOp",EDGE,"E18.filletArc"),sQuery(id+"F0.wireOp",EDGE,"E19.filletArc"),sQuery(id+"F0.wireOp",EDGE,"E20.filletArc"),sQuery(id+"F0.wireOp",EDGE,"E25.0"),sQuery(id+"F0.wireOp",EDGE,"E25.1"),sQuery(id+"F0.wireOp",EDGE,"E25.2"),sQuery(id+"F0.wireOp",EDGE,"E25.3"),sQuery(id+"F0.wireOp",EDGE,"E25.4"),sQuery(id+"F0.wireOp",EDGE,"E25.5"),sQuery(id+"F0.wireOp",EDGE,"E25.6"),sQuery(id+"F0.wireOp",EDGE,"E25.7")])],"isStart":false});
            extrude(context, id + "F18", {"entities" : qUnion([Q0, Q1, Q2]), "endBound" : BoundingType.UP_TO_SURFACE, "endBoundEntityFace" : qUnion([Q3]), "depth" : 25 * mm});
        }
    });
